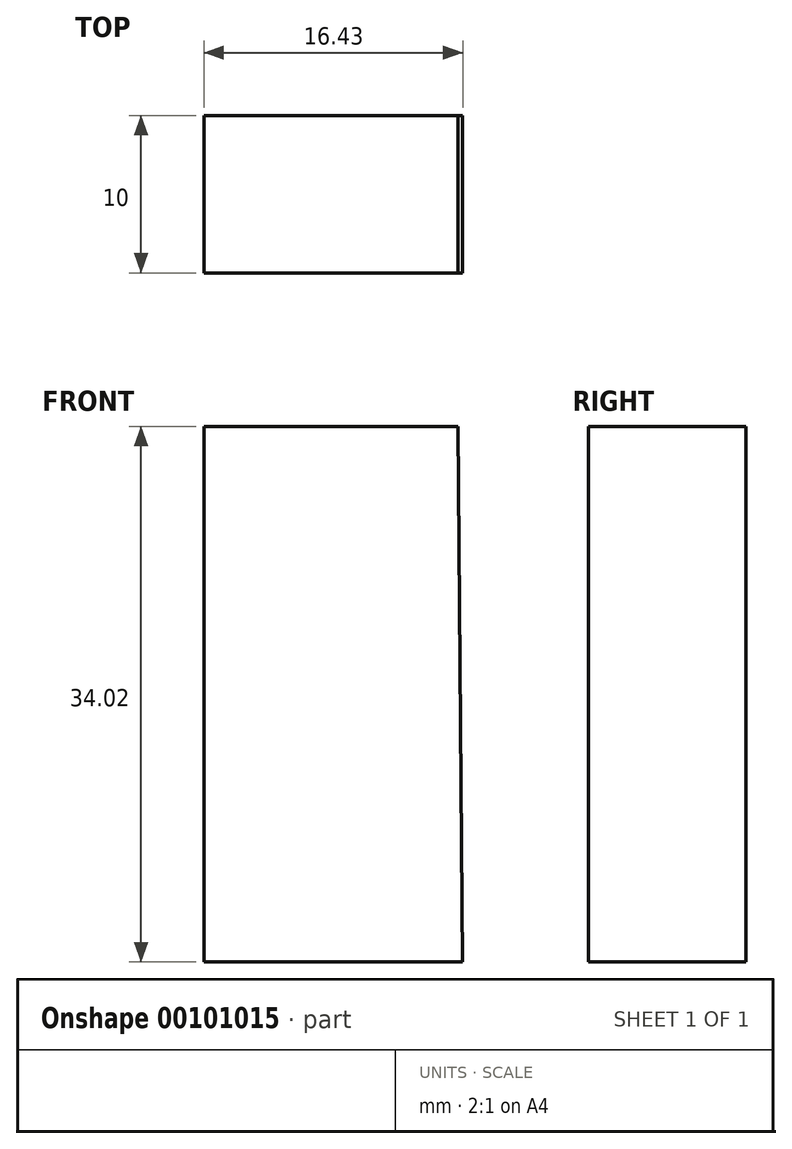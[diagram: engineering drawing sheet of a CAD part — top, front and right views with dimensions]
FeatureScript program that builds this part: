
annotation { "Feature Type Name" : "Feature", "Feature Type Description" : "" }
export const myFeature = defineFeature(function(context is Context, id is Id, definition is map)
    precondition{}
    {
        {
            var Q0;
            Q0=qCreatedBy(makeId("Front.planeOp"),FACE);
            var sketch = newSketch(context, id + "F0", { "sketchPlane" : qUnion([Q0])});
            skLineSegment(sketch, "E0", {"start": v(-39, 16.57) * mm, "end": v(-39, -17.45) * mm});
            skLineSegment(sketch, "E1", {"start": v(-39, -17.45) * mm, "end": v(-22.58, -17.45) * mm});
            skLineSegment(sketch, "E2", {"start": v(-39, 16.57) * mm, "end": v(-22.88, 16.57) * mm});
            skLineSegment(sketch, "E3", {"start": v(-22.88, 16.57) * mm, "end": v(-22.58, -17.45) * mm});
            skSolve(sketch);
        }
        {
            var Q0;
            Q0 = qSketchRegion(id + "F0", true);
            extrude(context, id + "F1", {"entities" : qUnion([Q0]), "endBound" : BoundingType.SYMMETRIC, "depth" : 10 * mm});
        }
        {
            var Q0;
            Q0=qCreatedBy(makeId("Front.planeOp"),FACE);
            cPlane(context, id + "F2", {"entities" : qUnion([Q0]), "cplaneType" : CPlaneType.OFFSET, "offset" : 10 * mm, "width" : 150 * mm, "height" : 150 * mm});
        }
    });
